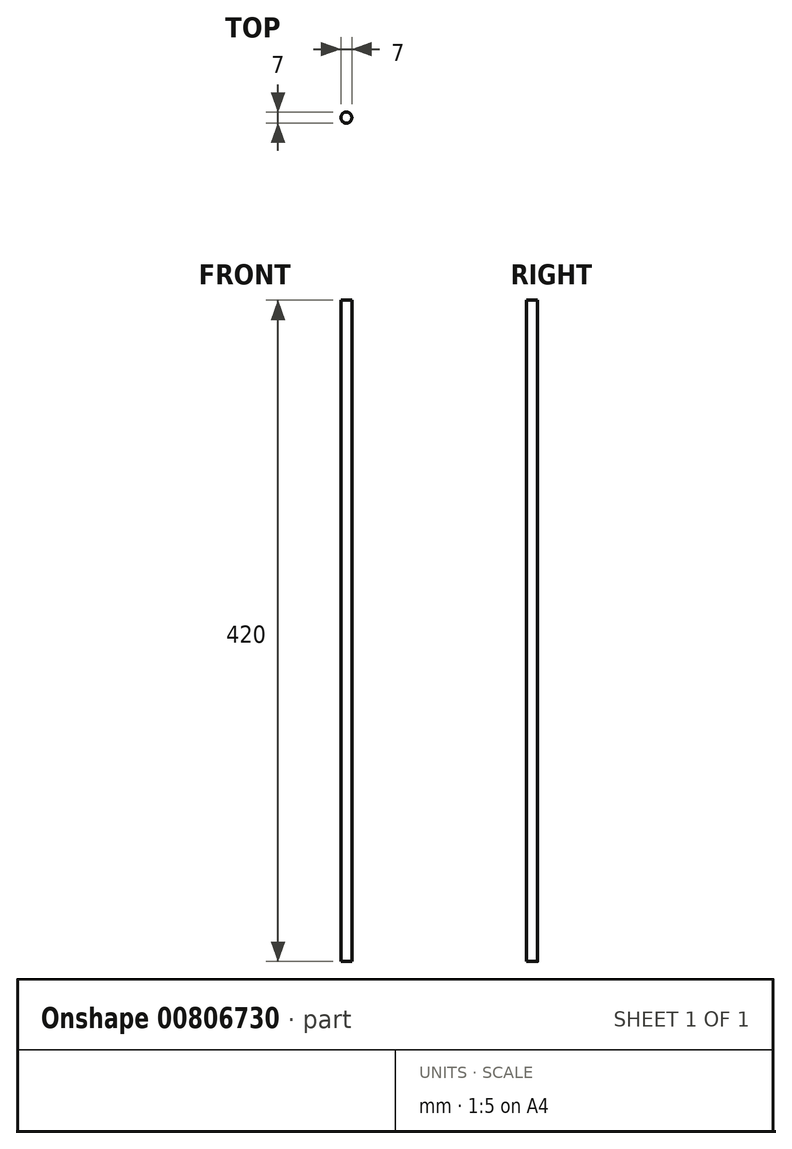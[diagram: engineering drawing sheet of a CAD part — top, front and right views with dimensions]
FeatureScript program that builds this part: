
annotation { "Feature Type Name" : "Feature", "Feature Type Description" : "" }
export const myFeature = defineFeature(function(context is Context, id is Id, definition is map)
    precondition{}
    {
        {
            var Q0;
            Q0=qCreatedBy(makeId("Top.planeOp"),FACE);
            var sketch = newSketch(context, id + "F0", { "sketchPlane" : qUnion([Q0])});
            skCircle(sketch, "E0", {"center": v(0, 0) * mm, "radius": 3.5 * mm});
            skSolve(sketch);
        }
        {
            var Q0;
            Q0=makeQuery(id+"F0.imprint","IMPRINT",FACE,{"disambiguationData":[TD([[makeQuery(id+"F0.imprint","IMPRINT",EDGE,{"derivedFrom":sQuery(id+"F0.wireOp",EDGE,"E0")}),1.0]])]});
            extrude(context, id + "F1", {"entities" : qUnion([Q0]), "depth" : 420 * mm, "offsetDistance" : 25 * mm});
        }
    });
